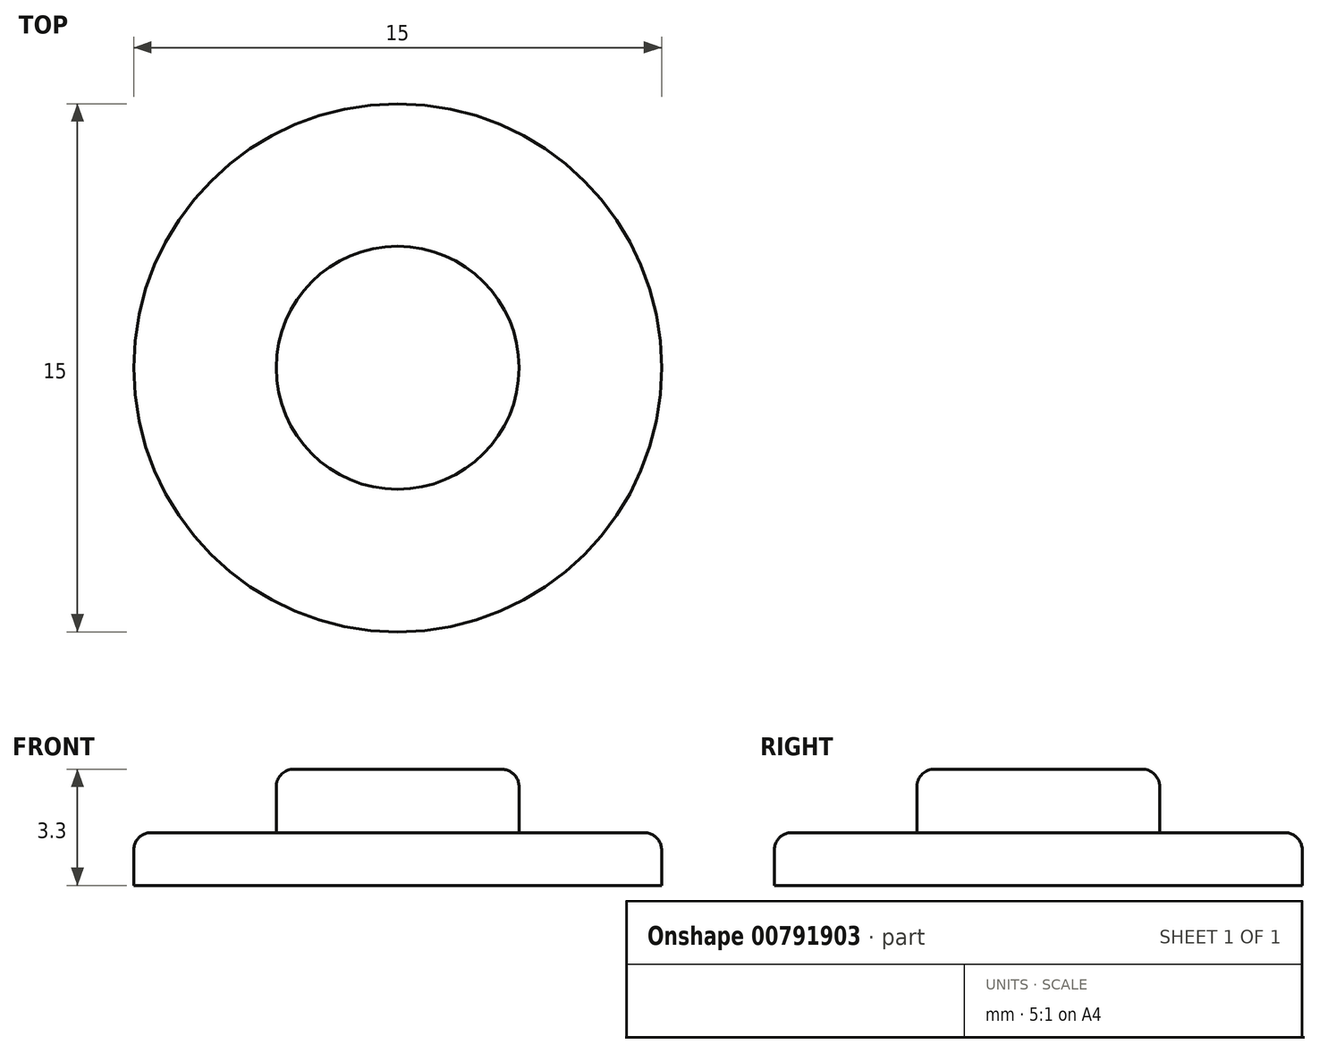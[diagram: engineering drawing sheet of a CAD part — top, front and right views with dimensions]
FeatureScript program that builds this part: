
annotation { "Feature Type Name" : "Feature", "Feature Type Description" : "" }
export const myFeature = defineFeature(function(context is Context, id is Id, definition is map)
    precondition{}
    {
        {
            var Q0;
            Q0=qCreatedBy(makeId("Top.planeOp"),FACE);
            var sketch = newSketch(context, id + "F0", { "sketchPlane" : qUnion([Q0])});
            skCircle(sketch, "E0", {"center": v(0, 0) * mm, "radius": 7.5 * mm});
            skSolve(sketch);
        }
        {
            var Q0;
            Q0 = qSketchRegion(id + "F0", true);
            extrude(context, id + "F1", {"entities" : qUnion([Q0]), "depth" : 1.5 * mm, "offsetDistance" : 25 * mm});
        }
        {
            var Q0;
            Q0=makeQuery(id+"F1.opExtrude","CAP_FACE",FACE,{"disambiguationData":[OSD([sQuery(id+"F0.wireOp",EDGE,"E0")])],"isStart":false});
            var sketch = newSketch(context, id + "F2", { "sketchPlane" : qUnion([Q0])});
            skCircle(sketch, "E1", {"center": v(0, 0) * mm, "radius": 3.45 * mm});
            skSolve(sketch);
        }
        {
            var Q0;
            Q0=makeQuery(id+"F2.imprint","IMPRINT",FACE,{"disambiguationData":[TD([[makeQuery(id+"F2.imprint","IMPRINT",EDGE,{"derivedFrom":sQuery(id+"F2.wireOp",EDGE,"E1")}),1.0]])]});
            extrude(context, id + "F3", {"entities" : qUnion([Q0]), "operationType" : NewBodyOperationType.ADD, "depth" : 1.8 * mm, "offsetDistance" : 25 * mm});
        }
        {
            var Q0;
            Q0=makeQuery(id+"F3.opExtrude","CAP_EDGE",EDGE,{"disambiguationData":[OSD([sQuery(id+"F2.wireOp",EDGE,"E1")])],"isStart":false});
            fillet(context, id + "F4", {"entities" : qUnion([Q0]), "radius" : .5 * mm, "tangentPropagation" : true, "allowEdgeOverflow" : false});
        }
        {
            var Q0;
            Q0=makeQuery(id+"F1.opExtrude","CAP_EDGE",EDGE,{"disambiguationData":[OSD([sQuery(id+"F0.wireOp",EDGE,"E0")])],"isStart":false});
            fillet(context, id + "F5", {"entities" : qUnion([Q0]), "radius" : .5 * mm, "tangentPropagation" : true, "allowEdgeOverflow" : false});
        }
    });
